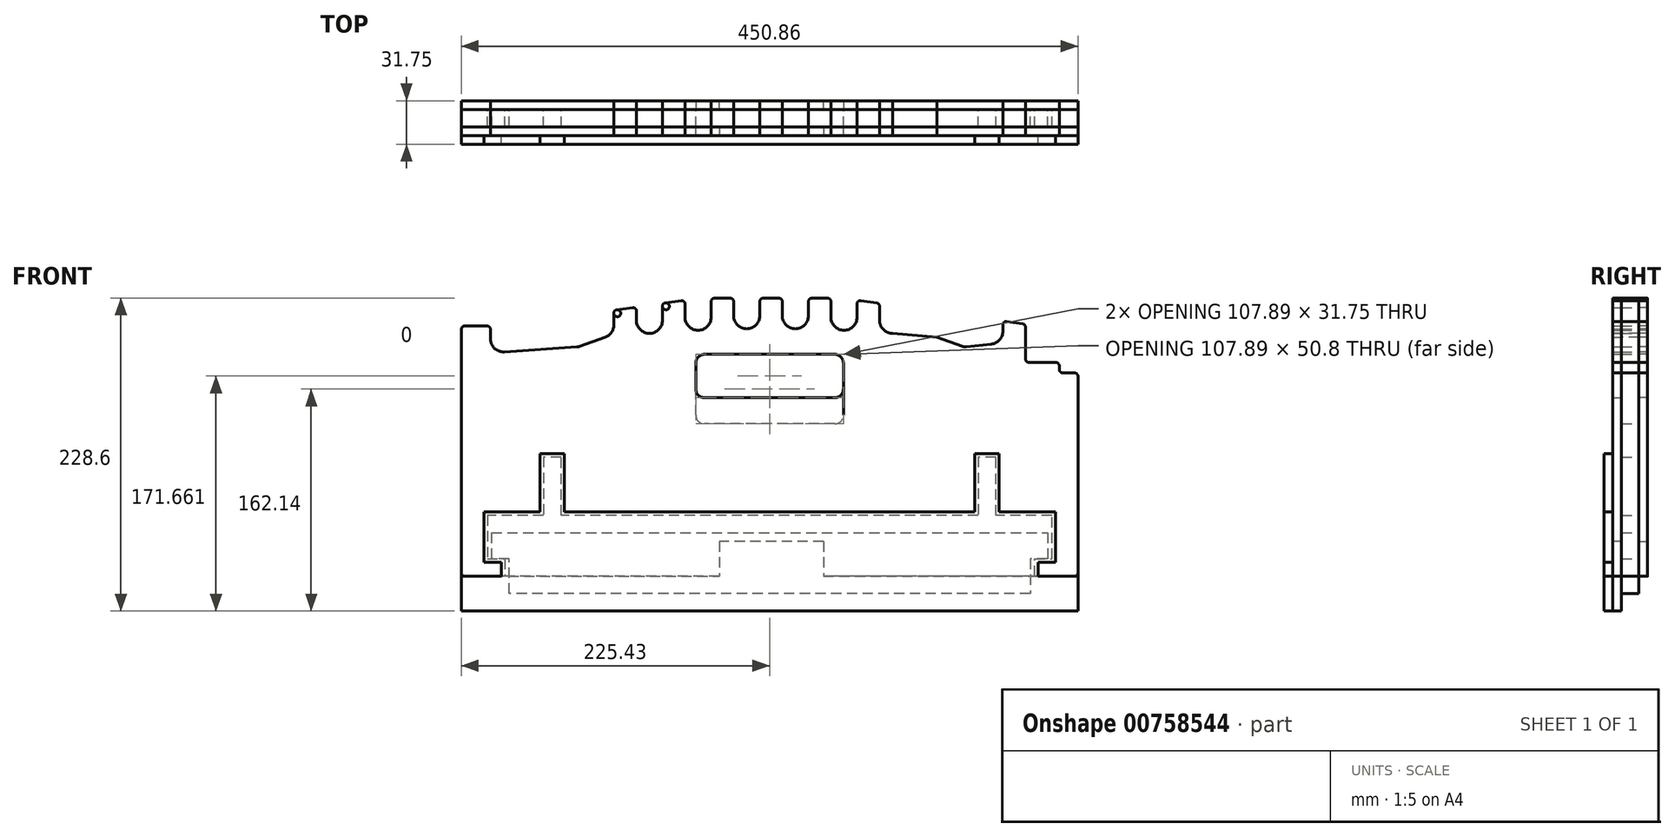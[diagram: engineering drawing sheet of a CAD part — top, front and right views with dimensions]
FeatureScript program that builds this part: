
annotation { "Feature Type Name" : "Feature", "Feature Type Description" : "" }
export const myFeature = defineFeature(function(context is Context, id is Id, definition is map)
    precondition{}
    {
        {
            var Q0;
            Q0=qCreatedBy(makeId("Front.planeOp"),FACE);
            var sketch = newSketch(context, id + "F0", { "sketchPlane" : qUnion([Q0])});
            skLineSegment(sketch, "E0", {"start": v(225.43, 44.45) * mm, "end": v(225.43, -101.6) * mm});
            skArc(sketch, "E1", {"start": v(225.42, 44.45) * mm, "mid": v(224.68, 46.25) * mm, "end": v(222.88, 47) * mm});
            skLineSegment(sketch, "E2", {"start": v(214.35, 47) * mm, "end": v(222.88, 47) * mm});
            skArc(sketch, "E3", {"start": v(211.8, 49.53) * mm, "mid": v(212.55, 47.73) * mm, "end": v(214.35, 47) * mm});
            skLineSegment(sketch, "E4", {"start": v(211.8, 52.07) * mm, "end": v(211.8, 49.53) * mm});
            skArc(sketch, "E5", {"start": v(211.8, 52.07) * mm, "mid": v(211.06, 53.87) * mm, "end": v(209.27, 54.6) * mm});
            skLineSegment(sketch, "E6", {"start": v(189.61, 54.61) * mm, "end": v(209.27, 54.61) * mm});
            skArc(sketch, "E7", {"start": v(187.07, 57.15) * mm, "mid": v(187.81, 55.35) * mm, "end": v(189.61, 54.61) * mm});
            skLineSegment(sketch, "E8", {"start": v(187.07, 80.43) * mm, "end": v(187.07, 57.15) * mm});
            skArc(sketch, "E9", {"start": v(187.07, 80.43) * mm, "mid": v(186.45, 82.1) * mm, "end": v(184.9, 82.94) * mm});
            skLineSegment(sketch, "E10", {"start": v(173.46, 84.58) * mm, "end": v(184.9, 82.94) * mm});
            skArc(sketch, "E11", {"start": v(173.46, 84.58) * mm, "mid": v(171.44, 83.98) * mm, "end": v(170.56, 82.06) * mm});
            skLineSegment(sketch, "E12", {"start": v(170.56, 77.52) * mm, "end": v(170.56, 82.06) * mm});
            skArc(sketch, "E13", {"start": v(162.11, 68.05) * mm, "mid": v(168.14, 71.17) * mm, "end": v(170.56, 77.52) * mm});
            skLineSegment(sketch, "E14", {"start": v(143.97, 65.99) * mm, "end": v(162.11, 68.05) * mm});
            skArc(sketch, "E15", {"start": v(141.12, 66.32) * mm, "mid": v(142.53, 65.99) * mm, "end": v(143.97, 65.99) * mm});
            skLineSegment(sketch, "E16", {"start": v(122.27, 73.06) * mm, "end": v(141.12, 66.32) * mm});
            skArc(sketch, "E17", {"start": v(115.95, 82.03) * mm, "mid": v(117.69, 76.54) * mm, "end": v(122.27, 73.06) * mm});
            skLineSegment(sketch, "E18", {"start": v(115.95, 90.6) * mm, "end": v(115.95, 82.03) * mm});
            skArc(sketch, "E19", {"start": v(115.95, 90.6) * mm, "mid": v(115.33, 92.26) * mm, "end": v(113.77, 93.1) * mm});
            skLineSegment(sketch, "E20", {"start": v(102.34, 94.74) * mm, "end": v(113.77, 93.1) * mm});
            skArc(sketch, "E21", {"start": v(102.34, 94.74) * mm, "mid": v(100.32, 94.14) * mm, "end": v(99.44, 92.22) * mm});
            skLineSegment(sketch, "E22", {"start": v(99.44, 85.4) * mm, "end": v(99.44, 92.22) * mm});
            skArc(sketch, "E23", {"start": v(80.4, 85.4) * mm, "mid": v(89.92, 75.87) * mm, "end": v(99.44, 85.4) * mm});
            skLineSegment(sketch, "E24", {"start": v(80.4, 95.67) * mm, "end": v(80.4, 85.4) * mm});
            skArc(sketch, "E25", {"start": v(80.4, 95.67) * mm, "mid": v(79.77, 97.34) * mm, "end": v(78.21, 98.19) * mm});
            skLineSegment(sketch, "E26", {"start": v(66.78, 99.82) * mm, "end": v(78.21, 98.19) * mm});
            skArc(sketch, "E27", {"start": v(66.78, 99.82) * mm, "mid": v(64.76, 99.22) * mm, "end": v(63.88, 97.3) * mm});
            skLineSegment(sketch, "E28", {"start": v(63.88, 87.64) * mm, "end": v(63.88, 97.3) * mm});
            skArc(sketch, "E29", {"start": v(44.83, 87.64) * mm, "mid": v(54.36, 78.12) * mm, "end": v(63.88, 87.64) * mm});
            skLineSegment(sketch, "E30", {"start": v(44.83, 99.06) * mm, "end": v(44.83, 87.64) * mm});
            skArc(sketch, "E31", {"start": v(44.83, 99.06) * mm, "mid": v(44.09, 100.86) * mm, "end": v(42.3, 101.6) * mm});
            skLineSegment(sketch, "E32", {"start": v(30.86, 101.6) * mm, "end": v(42.3, 101.6) * mm});
            skArc(sketch, "E33", {"start": v(30.86, 101.6) * mm, "mid": v(29.06, 100.86) * mm, "end": v(28.32, 99.06) * mm});
            skLineSegment(sketch, "E34", {"start": v(28.32, 88.76) * mm, "end": v(28.32, 99.06) * mm});
            skArc(sketch, "E35", {"start": v(9.27, 88.76) * mm, "mid": v(18.8, 79.24) * mm, "end": v(28.32, 88.76) * mm});
            skLineSegment(sketch, "E36", {"start": v(9.27, 99.06) * mm, "end": v(9.27, 88.76) * mm});
            skArc(sketch, "E37", {"start": v(9.27, 99.06) * mm, "mid": v(8.53, 100.86) * mm, "end": v(6.73, 101.6) * mm});
            skLineSegment(sketch, "E38", {"start": v(-4.7, 101.6) * mm, "end": v(6.73, 101.6) * mm});
            skArc(sketch, "E39", {"start": v(-4.7, 101.6) * mm, "mid": v(-6.5, 100.86) * mm, "end": v(-7.24, 99.06) * mm});
            skLineSegment(sketch, "E40", {"start": v(-7.24, 88.76) * mm, "end": v(-7.24, 99.06) * mm});
            skArc(sketch, "E41", {"start": v(-26.29, 88.76) * mm, "mid": v(-16.76, 79.24) * mm, "end": v(-7.24, 88.76) * mm});
            skLineSegment(sketch, "E42", {"start": v(-26.29, 99.06) * mm, "end": v(-26.29, 88.76) * mm});
            skArc(sketch, "E43", {"start": v(-26.29, 99.06) * mm, "mid": v(-27.03, 100.86) * mm, "end": v(-28.83, 101.6) * mm});
            skLineSegment(sketch, "E44", {"start": v(-40.26, 101.6) * mm, "end": v(-28.83, 101.6) * mm});
            skArc(sketch, "E45", {"start": v(-40.26, 101.6) * mm, "mid": v(-42.06, 100.86) * mm, "end": v(-42.8, 99.06) * mm});
            skLineSegment(sketch, "E46", {"start": v(-42.8, 87.64) * mm, "end": v(-42.8, 99.06) * mm});
            skArc(sketch, "E47", {"start": v(-61.85, 87.64) * mm, "mid": v(-52.32, 78.12) * mm, "end": v(-42.8, 87.64) * mm});
            skLineSegment(sketch, "E48", {"start": v(-61.85, 97.3) * mm, "end": v(-61.85, 87.64) * mm});
            skArc(sketch, "E49", {"start": v(-61.85, 97.3) * mm, "mid": v(-62.72, 99.23) * mm, "end": v(-64.75, 99.82) * mm});
            skLineSegment(sketch, "E50", {"start": v(-76.18, 98.19) * mm, "end": v(-64.75, 99.82) * mm});
            skArc(sketch, "E51", {"start": v(-76.18, 98.19) * mm, "mid": v(-77.74, 97.34) * mm, "end": v(-78.36, 95.67) * mm});
            skLineSegment(sketch, "E52", {"start": v(-78.36, 85.4) * mm, "end": v(-78.36, 95.67) * mm});
            skArc(sketch, "E53", {"start": v(-97.4, 85.4) * mm, "mid": v(-87.88, 75.87) * mm, "end": v(-78.36, 85.4) * mm});
            skLineSegment(sketch, "E54", {"start": v(-97.4, 92.23) * mm, "end": v(-97.4, 85.4) * mm});
            skArc(sketch, "E55", {"start": v(-97.4, 92.23) * mm, "mid": v(-98.28, 94.15) * mm, "end": v(-100.3, 94.74) * mm});
            skLineSegment(sketch, "E56", {"start": v(-111.74, 93.1) * mm, "end": v(-100.3, 94.74) * mm});
            skArc(sketch, "E57", {"start": v(-111.74, 93.1) * mm, "mid": v(-113.3, 92.26) * mm, "end": v(-113.92, 90.6) * mm});
            skLineSegment(sketch, "E58", {"start": v(-113.92, 82.03) * mm, "end": v(-113.92, 90.6) * mm});
            skArc(sketch, "E59", {"start": v(-120.24, 73.06) * mm, "mid": v(-115.66, 76.54) * mm, "end": v(-113.92, 82.03) * mm});
            skLineSegment(sketch, "E60", {"start": v(-139.09, 66.32) * mm, "end": v(-120.24, 73.06) * mm});
            skArc(sketch, "E61", {"start": v(-140.8, 65.96) * mm, "mid": v(-139.93, 66.08) * mm, "end": v(-139.09, 66.32) * mm});
            skLineSegment(sketch, "E62", {"start": v(-193.92, 62.35) * mm, "end": v(-140.8, 65.96) * mm});
            skArc(sketch, "E63", {"start": v(-204.09, 71.85) * mm, "mid": v(-201.07, 64.9) * mm, "end": v(-193.92, 62.35) * mm});
            skLineSegment(sketch, "E64", {"start": v(-204.09, 78.74) * mm, "end": v(-204.09, 71.85) * mm});
            skArc(sketch, "E65", {"start": v(-204.09, 78.74) * mm, "mid": v(-204.83, 80.54) * mm, "end": v(-206.63, 81.28) * mm});
            skLineSegment(sketch, "E66", {"start": v(-222.89, 81.28) * mm, "end": v(-206.63, 81.28) * mm});
            skArc(sketch, "E67", {"start": v(-222.89, 81.28) * mm, "mid": v(-224.68, 80.54) * mm, "end": v(-225.43, 78.74) * mm});
            skLineSegment(sketch, "E68", {"start": v(-225.43, -101.6) * mm, "end": v(-225.43, 78.74) * mm});
            skLineSegment(sketch, "E69", {"start": v(-193.68, -101.6) * mm, "end": v(-225.43, -101.6) * mm});
            skLineSegment(sketch, "E70", {"start": v(-193.68, -88.9) * mm, "end": v(-193.68, -101.6) * mm});
            skLineSegment(sketch, "E71", {"start": v(-206.38, -88.9) * mm, "end": v(-193.68, -88.9) * mm});
            skLineSegment(sketch, "E72", {"start": v(-206.38, -57.15) * mm, "end": v(-206.38, -88.9) * mm});
            skLineSegment(sketch, "E73", {"start": v(-165.35, -57.15) * mm, "end": v(-206.38, -57.15) * mm});
            skLineSegment(sketch, "E74", {"start": v(-165.35, -14.48) * mm, "end": v(-165.35, -57.15) * mm});
            skLineSegment(sketch, "E75", {"start": v(-152.4, -14.48) * mm, "end": v(-165.35, -14.48) * mm});
            skLineSegment(sketch, "E76", {"start": v(-152.4, -57.15) * mm, "end": v(-152.4, -14.48) * mm});
            skLineSegment(sketch, "E77", {"start": v(152.4, -57.15) * mm, "end": v(-152.4, -57.15) * mm});
            skLineSegment(sketch, "E78", {"start": v(152.4, -14.48) * mm, "end": v(152.4, -57.15) * mm});
            skLineSegment(sketch, "E79", {"start": v(165.35, -14.48) * mm, "end": v(152.4, -14.48) * mm});
            skLineSegment(sketch, "E80", {"start": v(165.35, -57.15) * mm, "end": v(165.35, -14.48) * mm});
            skLineSegment(sketch, "E81", {"start": v(206.38, -57.15) * mm, "end": v(165.35, -57.15) * mm});
            skLineSegment(sketch, "E82", {"start": v(206.38, -88.9) * mm, "end": v(206.38, -57.15) * mm});
            skLineSegment(sketch, "E83", {"start": v(193.68, -88.9) * mm, "end": v(206.38, -88.9) * mm});
            skLineSegment(sketch, "E84", {"start": v(193.68, -101.6) * mm, "end": v(193.68, -88.9) * mm});
            skLineSegment(sketch, "E85", {"start": v(225.43, -101.6) * mm, "end": v(193.68, -101.6) * mm});
            skLineSegment(sketch, "E86", {"start": v(47.6, 9.74) * mm, "end": v(-47.6, 9.74) * mm});
            skArc(sketch, "E87", {"start": v(-53.95, 16.1) * mm, "mid": v(-52.09, 11.6) * mm, "end": v(-47.6, 9.74) * mm});
            skLineSegment(sketch, "E88", {"start": v(-53.95, 16.1) * mm, "end": v(-53.95, 54.2) * mm});
            skArc(sketch, "E89", {"start": v(-47.6, 60.54) * mm, "mid": v(-52.09, 58.68) * mm, "end": v(-53.95, 54.2) * mm});
            skLineSegment(sketch, "E90", {"start": v(-47.6, 60.54) * mm, "end": v(47.6, 60.54) * mm});
            skArc(sketch, "E91", {"start": v(53.95, 54.2) * mm, "mid": v(52.09, 58.68) * mm, "end": v(47.6, 60.54) * mm});
            skLineSegment(sketch, "E92", {"start": v(53.95, 54.2) * mm, "end": v(53.95, 16.1) * mm});
            skArc(sketch, "E93", {"start": v(47.6, 9.74) * mm, "mid": v(52.09, 11.6) * mm, "end": v(53.95, 16.1) * mm});
            skLineSegment(sketch, "E94", {"start": v(225.43, -101.6) * mm, "end": v(-225.43, -101.6) * mm, "construction": true});
            skLineSegment(sketch, "E95", {"start": v(-225.43, -101.6) * mm, "end": v(-225.43, 0) * mm, "construction": true});
            skLineSegment(sketch, "E96", {"start": v(-225.43, 0) * mm, "end": v(225.43, 0) * mm, "construction": true});
            skLineSegment(sketch, "E97", {"start": v(225.43, 0) * mm, "end": v(225.43, -101.6) * mm, "construction": true});
            skSolve(sketch);
        }
        {
            var Q0;
            Q0=qSketchRegion(id+"F0",true);
            extrude(context, id + "F1", {"entities" : qUnion([Q0]), "depth" : 12.7 * mm});
        }
        {
            var Q0;
            Q0=makeQuery(id+"F1.opExtrude","CAP_FACE",FACE,{"disambiguationData":[OSD([sQuery(id+"F0.wireOp",EDGE,"f3b8bc04-095d-494a-bcce-8306202adf07"),sQuery(id+"F0.wireOp",EDGE,"08e92012-2e21-4d94-9f0a-c8e57075e395"),sQuery(id+"F0.wireOp",EDGE,"122fa739-26d1-4298-ae19-82ac91bd4e23"),sQuery(id+"F0.wireOp",EDGE,"d5e32c5b-27bd-42dd-9b3f-d947ba78b5c6"),sQuery(id+"F0.wireOp",EDGE,"E0"),sQuery(id+"F0.wireOp",EDGE,"E1"),sQuery(id+"F0.wireOp",EDGE,"E2"),sQuery(id+"F0.wireOp",EDGE,"E3"),sQuery(id+"F0.wireOp",EDGE,"E4"),sQuery(id+"F0.wireOp",EDGE,"E5"),sQuery(id+"F0.wireOp",EDGE,"E6"),sQuery(id+"F0.wireOp",EDGE,"E7"),sQuery(id+"F0.wireOp",EDGE,"E8"),sQuery(id+"F0.wireOp",EDGE,"E9"),sQuery(id+"F0.wireOp",EDGE,"E10"),sQuery(id+"F0.wireOp",EDGE,"E11"),sQuery(id+"F0.wireOp",EDGE,"E12"),sQuery(id+"F0.wireOp",EDGE,"E13"),sQuery(id+"F0.wireOp",EDGE,"E14"),sQuery(id+"F0.wireOp",EDGE,"E15"),sQuery(id+"F0.wireOp",EDGE,"E16"),sQuery(id+"F0.wireOp",EDGE,"E17"),sQuery(id+"F0.wireOp",EDGE,"E18"),sQuery(id+"F0.wireOp",EDGE,"E19"),sQuery(id+"F0.wireOp",EDGE,"E20"),sQuery(id+"F0.wireOp",EDGE,"E21"),sQuery(id+"F0.wireOp",EDGE,"E22"),sQuery(id+"F0.wireOp",EDGE,"E23"),sQuery(id+"F0.wireOp",EDGE,"E24"),sQuery(id+"F0.wireOp",EDGE,"E25"),sQuery(id+"F0.wireOp",EDGE,"E26"),sQuery(id+"F0.wireOp",EDGE,"E27"),sQuery(id+"F0.wireOp",EDGE,"E28"),sQuery(id+"F0.wireOp",EDGE,"E29"),sQuery(id+"F0.wireOp",EDGE,"E30"),sQuery(id+"F0.wireOp",EDGE,"E31"),sQuery(id+"F0.wireOp",EDGE,"E32"),sQuery(id+"F0.wireOp",EDGE,"E33"),sQuery(id+"F0.wireOp",EDGE,"E34"),sQuery(id+"F0.wireOp",EDGE,"E35"),sQuery(id+"F0.wireOp",EDGE,"E36"),sQuery(id+"F0.wireOp",EDGE,"E37"),sQuery(id+"F0.wireOp",EDGE,"E38"),sQuery(id+"F0.wireOp",EDGE,"E39"),sQuery(id+"F0.wireOp",EDGE,"E40"),sQuery(id+"F0.wireOp",EDGE,"E41"),sQuery(id+"F0.wireOp",EDGE,"E42"),sQuery(id+"F0.wireOp",EDGE,"E43"),sQuery(id+"F0.wireOp",EDGE,"E44"),sQuery(id+"F0.wireOp",EDGE,"E45"),sQuery(id+"F0.wireOp",EDGE,"E46"),sQuery(id+"F0.wireOp",EDGE,"E47"),sQuery(id+"F0.wireOp",EDGE,"E48"),sQuery(id+"F0.wireOp",EDGE,"E49"),sQuery(id+"F0.wireOp",EDGE,"E50"),sQuery(id+"F0.wireOp",EDGE,"E51"),sQuery(id+"F0.wireOp",EDGE,"E52"),sQuery(id+"F0.wireOp",EDGE,"E53"),sQuery(id+"F0.wireOp",EDGE,"E54"),sQuery(id+"F0.wireOp",EDGE,"E55"),sQuery(id+"F0.wireOp",EDGE,"E56"),sQuery(id+"F0.wireOp",EDGE,"E57"),sQuery(id+"F0.wireOp",EDGE,"E58"),sQuery(id+"F0.wireOp",EDGE,"E59"),sQuery(id+"F0.wireOp",EDGE,"E60"),sQuery(id+"F0.wireOp",EDGE,"E61"),sQuery(id+"F0.wireOp",EDGE,"E62"),sQuery(id+"F0.wireOp",EDGE,"E63"),sQuery(id+"F0.wireOp",EDGE,"E64"),sQuery(id+"F0.wireOp",EDGE,"E65"),sQuery(id+"F0.wireOp",EDGE,"E66"),sQuery(id+"F0.wireOp",EDGE,"E67"),sQuery(id+"F0.wireOp",EDGE,"E68"),sQuery(id+"F0.wireOp",EDGE,"E69"),sQuery(id+"F0.wireOp",EDGE,"E70"),sQuery(id+"F0.wireOp",EDGE,"E71"),sQuery(id+"F0.wireOp",EDGE,"E72"),sQuery(id+"F0.wireOp",EDGE,"E73"),sQuery(id+"F0.wireOp",EDGE,"E74"),sQuery(id+"F0.wireOp",EDGE,"E75"),sQuery(id+"F0.wireOp",EDGE,"E76"),sQuery(id+"F0.wireOp",EDGE,"E77"),sQuery(id+"F0.wireOp",EDGE,"E78"),sQuery(id+"F0.wireOp",EDGE,"E79"),sQuery(id+"F0.wireOp",EDGE,"E80"),sQuery(id+"F0.wireOp",EDGE,"E81"),sQuery(id+"F0.wireOp",EDGE,"E82"),sQuery(id+"F0.wireOp",EDGE,"E83"),sQuery(id+"F0.wireOp",EDGE,"E84"),sQuery(id+"F0.wireOp",EDGE,"E85"),sQuery(id+"F0.wireOp",EDGE,"2d70706d-4c91-45b7-b293-bf747273fc1e"),sQuery(id+"F0.wireOp",EDGE,"f606c3c6-6e26-49ba-bb4a-ffbf22b89f78"),sQuery(id+"F0.wireOp",EDGE,"6ded5a20-7a3f-46e3-8459-1bb58dbc2f72"),sQuery(id+"F0.wireOp",EDGE,"099ca5a8-81e7-49d1-b38d-3a86f93f5891"),sQuery(id+"F0.wireOp",EDGE,"E86"),sQuery(id+"F0.wireOp",EDGE,"E87"),sQuery(id+"F0.wireOp",EDGE,"E88"),sQuery(id+"F0.wireOp",EDGE,"E89"),sQuery(id+"F0.wireOp",EDGE,"E90"),sQuery(id+"F0.wireOp",EDGE,"E91"),sQuery(id+"F0.wireOp",EDGE,"E92"),sQuery(id+"F0.wireOp",EDGE,"E93")])],"isStart":true});
            cPlane(context, id + "F2", {"entities" : qUnion([Q0]), "cplaneType" : CPlaneType.OFFSET, "offset" : 0 * mm, "oppositeDirection" : true, "width" : 152.4 * mm, "height" : 152.4 * mm});
        }
        {
            var Q0;
            Q0=qCreatedBy(id+"F2.planeOp",FACE);
            var sketch = newSketch(context, id + "F3", { "sketchPlane" : qUnion([Q0])});
            skLineSegment(sketch, "E98", {"start": v(-203.2, -69.85) * mm, "end": v(-203.2, -88.9) * mm});
            skLineSegment(sketch, "E99", {"start": v(-203.2, -88.9) * mm, "end": v(-190.5, -88.9) * mm});
            skLineSegment(sketch, "E100", {"start": v(-190.5, -88.9) * mm, "end": v(-190.5, -114.3) * mm});
            skLineSegment(sketch, "E101", {"start": v(-190.5, -114.3) * mm, "end": v(190.5, -114.3) * mm});
            skLineSegment(sketch, "E102", {"start": v(190.5, -114.3) * mm, "end": v(190.5, -88.9) * mm});
            skLineSegment(sketch, "E103", {"start": v(190.5, -88.9) * mm, "end": v(203.2, -88.9) * mm});
            skLineSegment(sketch, "E104", {"start": v(203.2, -88.9) * mm, "end": v(203.2, -69.85) * mm});
            skLineSegment(sketch, "E105", {"start": v(203.2, -69.85) * mm, "end": v(-203.2, -69.85) * mm});
            skSolve(sketch);
        }
        {
            var Q0;
            Q0=qSketchRegion(id+"F3",true);
            extrude(context, id + "F4", {"entities" : qUnion([Q0]), "oppositeDirection" : true, "depth" : 12.7 * mm});
        }
        {
            var Q0;
            Q0=makeQuery(id+"F1.opExtrude","CAP_FACE",FACE,{"disambiguationData":[OSD([sQuery(id+"F0.wireOp",EDGE,"f3b8bc04-095d-494a-bcce-8306202adf07"),sQuery(id+"F0.wireOp",EDGE,"08e92012-2e21-4d94-9f0a-c8e57075e395"),sQuery(id+"F0.wireOp",EDGE,"122fa739-26d1-4298-ae19-82ac91bd4e23"),sQuery(id+"F0.wireOp",EDGE,"d5e32c5b-27bd-42dd-9b3f-d947ba78b5c6"),sQuery(id+"F0.wireOp",EDGE,"E0"),sQuery(id+"F0.wireOp",EDGE,"E1"),sQuery(id+"F0.wireOp",EDGE,"E2"),sQuery(id+"F0.wireOp",EDGE,"E3"),sQuery(id+"F0.wireOp",EDGE,"E4"),sQuery(id+"F0.wireOp",EDGE,"E5"),sQuery(id+"F0.wireOp",EDGE,"E6"),sQuery(id+"F0.wireOp",EDGE,"E7"),sQuery(id+"F0.wireOp",EDGE,"E8"),sQuery(id+"F0.wireOp",EDGE,"E9"),sQuery(id+"F0.wireOp",EDGE,"E10"),sQuery(id+"F0.wireOp",EDGE,"E11"),sQuery(id+"F0.wireOp",EDGE,"E12"),sQuery(id+"F0.wireOp",EDGE,"E13"),sQuery(id+"F0.wireOp",EDGE,"E14"),sQuery(id+"F0.wireOp",EDGE,"E15"),sQuery(id+"F0.wireOp",EDGE,"E16"),sQuery(id+"F0.wireOp",EDGE,"E17"),sQuery(id+"F0.wireOp",EDGE,"E18"),sQuery(id+"F0.wireOp",EDGE,"E19"),sQuery(id+"F0.wireOp",EDGE,"E20"),sQuery(id+"F0.wireOp",EDGE,"E21"),sQuery(id+"F0.wireOp",EDGE,"E22"),sQuery(id+"F0.wireOp",EDGE,"E23"),sQuery(id+"F0.wireOp",EDGE,"E24"),sQuery(id+"F0.wireOp",EDGE,"E25"),sQuery(id+"F0.wireOp",EDGE,"E26"),sQuery(id+"F0.wireOp",EDGE,"E27"),sQuery(id+"F0.wireOp",EDGE,"E28"),sQuery(id+"F0.wireOp",EDGE,"E29"),sQuery(id+"F0.wireOp",EDGE,"E30"),sQuery(id+"F0.wireOp",EDGE,"E31"),sQuery(id+"F0.wireOp",EDGE,"E32"),sQuery(id+"F0.wireOp",EDGE,"E33"),sQuery(id+"F0.wireOp",EDGE,"E34"),sQuery(id+"F0.wireOp",EDGE,"E35"),sQuery(id+"F0.wireOp",EDGE,"E36"),sQuery(id+"F0.wireOp",EDGE,"E37"),sQuery(id+"F0.wireOp",EDGE,"E38"),sQuery(id+"F0.wireOp",EDGE,"E39"),sQuery(id+"F0.wireOp",EDGE,"E40"),sQuery(id+"F0.wireOp",EDGE,"E41"),sQuery(id+"F0.wireOp",EDGE,"E42"),sQuery(id+"F0.wireOp",EDGE,"E43"),sQuery(id+"F0.wireOp",EDGE,"E44"),sQuery(id+"F0.wireOp",EDGE,"E45"),sQuery(id+"F0.wireOp",EDGE,"E46"),sQuery(id+"F0.wireOp",EDGE,"E47"),sQuery(id+"F0.wireOp",EDGE,"E48"),sQuery(id+"F0.wireOp",EDGE,"E49"),sQuery(id+"F0.wireOp",EDGE,"E50"),sQuery(id+"F0.wireOp",EDGE,"E51"),sQuery(id+"F0.wireOp",EDGE,"E52"),sQuery(id+"F0.wireOp",EDGE,"E53"),sQuery(id+"F0.wireOp",EDGE,"E54"),sQuery(id+"F0.wireOp",EDGE,"E55"),sQuery(id+"F0.wireOp",EDGE,"E56"),sQuery(id+"F0.wireOp",EDGE,"E57"),sQuery(id+"F0.wireOp",EDGE,"E58"),sQuery(id+"F0.wireOp",EDGE,"E59"),sQuery(id+"F0.wireOp",EDGE,"E60"),sQuery(id+"F0.wireOp",EDGE,"E61"),sQuery(id+"F0.wireOp",EDGE,"E62"),sQuery(id+"F0.wireOp",EDGE,"E63"),sQuery(id+"F0.wireOp",EDGE,"E64"),sQuery(id+"F0.wireOp",EDGE,"E65"),sQuery(id+"F0.wireOp",EDGE,"E66"),sQuery(id+"F0.wireOp",EDGE,"E67"),sQuery(id+"F0.wireOp",EDGE,"E68"),sQuery(id+"F0.wireOp",EDGE,"E69"),sQuery(id+"F0.wireOp",EDGE,"E70"),sQuery(id+"F0.wireOp",EDGE,"E71"),sQuery(id+"F0.wireOp",EDGE,"E72"),sQuery(id+"F0.wireOp",EDGE,"E73"),sQuery(id+"F0.wireOp",EDGE,"E74"),sQuery(id+"F0.wireOp",EDGE,"E75"),sQuery(id+"F0.wireOp",EDGE,"E76"),sQuery(id+"F0.wireOp",EDGE,"E77"),sQuery(id+"F0.wireOp",EDGE,"E78"),sQuery(id+"F0.wireOp",EDGE,"E79"),sQuery(id+"F0.wireOp",EDGE,"E80"),sQuery(id+"F0.wireOp",EDGE,"E81"),sQuery(id+"F0.wireOp",EDGE,"E82"),sQuery(id+"F0.wireOp",EDGE,"E83"),sQuery(id+"F0.wireOp",EDGE,"E84"),sQuery(id+"F0.wireOp",EDGE,"E85"),sQuery(id+"F0.wireOp",EDGE,"2d70706d-4c91-45b7-b293-bf747273fc1e"),sQuery(id+"F0.wireOp",EDGE,"f606c3c6-6e26-49ba-bb4a-ffbf22b89f78"),sQuery(id+"F0.wireOp",EDGE,"6ded5a20-7a3f-46e3-8459-1bb58dbc2f72"),sQuery(id+"F0.wireOp",EDGE,"099ca5a8-81e7-49d1-b38d-3a86f93f5891"),sQuery(id+"F0.wireOp",EDGE,"E86"),sQuery(id+"F0.wireOp",EDGE,"E87"),sQuery(id+"F0.wireOp",EDGE,"E88"),sQuery(id+"F0.wireOp",EDGE,"E89"),sQuery(id+"F0.wireOp",EDGE,"E90"),sQuery(id+"F0.wireOp",EDGE,"E91"),sQuery(id+"F0.wireOp",EDGE,"E92"),sQuery(id+"F0.wireOp",EDGE,"E93")])],"isStart":true});
            cPlane(context, id + "F5", {"entities" : qUnion([Q0]), "cplaneType" : CPlaneType.OFFSET, "offset" : 6.35 * mm, "oppositeDirection" : true, "width" : 152.4 * mm, "height" : 152.4 * mm});
        }
        {
            var Q0;
            Q0=qCreatedBy(id+"F2.planeOp",FACE);
            var sketch = newSketch(context, id + "F6", { "sketchPlane" : qUnion([Q0])});
            skLineSegment(sketch, "E106", {"start": v(-225.43, 44.45) * mm, "end": v(-225.43, -99.06) * mm});
            skArc(sketch, "E107", {"start": v(-225.43, -99.06) * mm, "mid": v(-224.68, -100.86) * mm, "end": v(-222.89, -101.6) * mm});
            skLineSegment(sketch, "E108", {"start": v(-222.89, -101.6) * mm, "end": v(222.88, -101.6) * mm});
            skArc(sketch, "E109", {"start": v(222.88, -101.6) * mm, "mid": v(224.68, -100.86) * mm, "end": v(225.42, -99.06) * mm});
            skLineSegment(sketch, "E110", {"start": v(225.43, -99.06) * mm, "end": v(225.43, 78.74) * mm});
            skArc(sketch, "E111", {"start": v(225.42, 78.74) * mm, "mid": v(224.68, 80.54) * mm, "end": v(222.88, 81.28) * mm});
            skLineSegment(sketch, "E112", {"start": v(222.88, 81.28) * mm, "end": v(206.63, 81.28) * mm});
            skArc(sketch, "E113", {"start": v(206.63, 81.28) * mm, "mid": v(204.83, 80.54) * mm, "end": v(204.09, 78.74) * mm});
            skLineSegment(sketch, "E114", {"start": v(204.09, 78.74) * mm, "end": v(204.09, 71.85) * mm});
            skArc(sketch, "E115", {"start": v(193.92, 62.35) * mm, "mid": v(201.07, 64.9) * mm, "end": v(204.09, 71.85) * mm});
            skLineSegment(sketch, "E116", {"start": v(193.92, 62.35) * mm, "end": v(140.8, 65.96) * mm});
            skArc(sketch, "E117", {"start": v(139.09, 66.32) * mm, "mid": v(139.93, 66.08) * mm, "end": v(140.8, 65.96) * mm});
            skLineSegment(sketch, "E118", {"start": v(139.09, 66.32) * mm, "end": v(120.24, 73.06) * mm});
            skArc(sketch, "E119", {"start": v(113.92, 82.03) * mm, "mid": v(115.66, 76.54) * mm, "end": v(120.24, 73.06) * mm});
            skLineSegment(sketch, "E120", {"start": v(113.92, 82.03) * mm, "end": v(113.92, 90.6) * mm});
            skArc(sketch, "E121", {"start": v(113.92, 90.6) * mm, "mid": v(113.3, 92.26) * mm, "end": v(111.74, 93.1) * mm});
            skLineSegment(sketch, "E122", {"start": v(111.74, 93.1) * mm, "end": v(100.3, 94.74) * mm});
            skArc(sketch, "E123", {"start": v(100.3, 94.74) * mm, "mid": v(98.28, 94.15) * mm, "end": v(97.4, 92.23) * mm});
            skLineSegment(sketch, "E124", {"start": v(97.4, 92.23) * mm, "end": v(97.4, 85.4) * mm});
            skArc(sketch, "E125", {"start": v(78.36, 85.4) * mm, "mid": v(87.88, 75.87) * mm, "end": v(97.4, 85.4) * mm});
            skLineSegment(sketch, "E126", {"start": v(78.36, 85.4) * mm, "end": v(78.36, 95.67) * mm});
            skArc(sketch, "E127", {"start": v(78.36, 95.67) * mm, "mid": v(77.74, 97.34) * mm, "end": v(76.18, 98.19) * mm});
            skLineSegment(sketch, "E128", {"start": v(76.18, 98.19) * mm, "end": v(64.75, 99.82) * mm});
            skArc(sketch, "E129", {"start": v(64.75, 99.82) * mm, "mid": v(62.72, 99.23) * mm, "end": v(61.85, 97.3) * mm});
            skLineSegment(sketch, "E130", {"start": v(61.85, 97.3) * mm, "end": v(61.85, 87.64) * mm});
            skArc(sketch, "E131", {"start": v(42.8, 87.64) * mm, "mid": v(52.32, 78.12) * mm, "end": v(61.85, 87.64) * mm});
            skLineSegment(sketch, "E132", {"start": v(42.8, 87.64) * mm, "end": v(42.8, 99.06) * mm});
            skArc(sketch, "E133", {"start": v(42.8, 99.06) * mm, "mid": v(42.06, 100.86) * mm, "end": v(40.26, 101.6) * mm});
            skLineSegment(sketch, "E134", {"start": v(40.26, 101.6) * mm, "end": v(28.83, 101.6) * mm});
            skArc(sketch, "E135", {"start": v(28.83, 101.6) * mm, "mid": v(27.03, 100.86) * mm, "end": v(26.29, 99.06) * mm});
            skLineSegment(sketch, "E136", {"start": v(26.29, 99.06) * mm, "end": v(26.29, 88.76) * mm});
            skArc(sketch, "E137", {"start": v(7.24, 88.76) * mm, "mid": v(16.76, 79.24) * mm, "end": v(26.29, 88.76) * mm});
            skLineSegment(sketch, "E138", {"start": v(7.24, 88.76) * mm, "end": v(7.24, 99.06) * mm});
            skArc(sketch, "E139", {"start": v(7.24, 99.06) * mm, "mid": v(6.5, 100.86) * mm, "end": v(4.7, 101.6) * mm});
            skLineSegment(sketch, "E140", {"start": v(4.7, 101.6) * mm, "end": v(-6.73, 101.6) * mm});
            skArc(sketch, "E141", {"start": v(-6.73, 101.6) * mm, "mid": v(-8.53, 100.86) * mm, "end": v(-9.27, 99.06) * mm});
            skLineSegment(sketch, "E142", {"start": v(-9.27, 99.06) * mm, "end": v(-9.27, 88.76) * mm});
            skArc(sketch, "E143", {"start": v(-28.32, 88.76) * mm, "mid": v(-18.8, 79.24) * mm, "end": v(-9.27, 88.76) * mm});
            skLineSegment(sketch, "E144", {"start": v(-28.32, 88.76) * mm, "end": v(-28.32, 99.06) * mm});
            skArc(sketch, "E145", {"start": v(-28.32, 99.06) * mm, "mid": v(-29.06, 100.86) * mm, "end": v(-30.86, 101.6) * mm});
            skLineSegment(sketch, "E146", {"start": v(-30.86, 101.6) * mm, "end": v(-42.3, 101.6) * mm});
            skArc(sketch, "E147", {"start": v(-42.3, 101.6) * mm, "mid": v(-44.09, 100.86) * mm, "end": v(-44.83, 99.06) * mm});
            skLineSegment(sketch, "E148", {"start": v(-44.83, 99.06) * mm, "end": v(-44.83, 87.64) * mm});
            skArc(sketch, "E149", {"start": v(-63.88, 87.64) * mm, "mid": v(-54.36, 78.12) * mm, "end": v(-44.83, 87.64) * mm});
            skLineSegment(sketch, "E150", {"start": v(-63.88, 87.64) * mm, "end": v(-63.88, 97.3) * mm});
            skArc(sketch, "E151", {"start": v(-63.88, 97.3) * mm, "mid": v(-64.76, 99.22) * mm, "end": v(-66.78, 99.82) * mm});
            skLineSegment(sketch, "E152", {"start": v(-66.78, 99.82) * mm, "end": v(-78.21, 98.19) * mm});
            skArc(sketch, "E153", {"start": v(-78.21, 98.19) * mm, "mid": v(-79.77, 97.34) * mm, "end": v(-80.4, 95.67) * mm});
            skLineSegment(sketch, "E154", {"start": v(-80.4, 95.67) * mm, "end": v(-80.4, 85.4) * mm});
            skArc(sketch, "E155", {"start": v(-99.44, 85.4) * mm, "mid": v(-89.92, 75.87) * mm, "end": v(-80.4, 85.4) * mm});
            skLineSegment(sketch, "E156", {"start": v(-99.44, 85.4) * mm, "end": v(-99.44, 92.22) * mm});
            skArc(sketch, "E157", {"start": v(-99.44, 92.22) * mm, "mid": v(-100.32, 94.14) * mm, "end": v(-102.34, 94.74) * mm});
            skLineSegment(sketch, "E158", {"start": v(-102.34, 94.74) * mm, "end": v(-113.77, 93.1) * mm});
            skArc(sketch, "E159", {"start": v(-113.77, 93.1) * mm, "mid": v(-115.33, 92.26) * mm, "end": v(-115.95, 90.6) * mm});
            skLineSegment(sketch, "E160", {"start": v(-115.95, 90.6) * mm, "end": v(-115.95, 82.03) * mm});
            skArc(sketch, "E161", {"start": v(-122.27, 73.06) * mm, "mid": v(-117.69, 76.54) * mm, "end": v(-115.95, 82.03) * mm});
            skLineSegment(sketch, "E162", {"start": v(-122.27, 73.06) * mm, "end": v(-141.12, 66.32) * mm});
            skArc(sketch, "E163", {"start": v(-143.97, 65.99) * mm, "mid": v(-142.53, 65.99) * mm, "end": v(-141.12, 66.32) * mm});
            skLineSegment(sketch, "E164", {"start": v(-143.97, 65.99) * mm, "end": v(-162.11, 68.05) * mm});
            skArc(sketch, "E165", {"start": v(-170.56, 77.52) * mm, "mid": v(-168.14, 71.17) * mm, "end": v(-162.11, 68.05) * mm});
            skLineSegment(sketch, "E166", {"start": v(-170.56, 77.52) * mm, "end": v(-170.56, 82.06) * mm});
            skArc(sketch, "E167", {"start": v(-170.56, 82.06) * mm, "mid": v(-171.44, 83.98) * mm, "end": v(-173.46, 84.58) * mm});
            skLineSegment(sketch, "E168", {"start": v(-173.46, 84.58) * mm, "end": v(-184.9, 82.94) * mm});
            skArc(sketch, "E169", {"start": v(-184.9, 82.94) * mm, "mid": v(-186.45, 82.1) * mm, "end": v(-187.07, 80.43) * mm});
            skLineSegment(sketch, "E170", {"start": v(-187.07, 80.43) * mm, "end": v(-187.07, 57.15) * mm});
            skArc(sketch, "E171", {"start": v(-189.61, 54.61) * mm, "mid": v(-187.81, 55.35) * mm, "end": v(-187.07, 57.15) * mm});
            skLineSegment(sketch, "E172", {"start": v(-189.61, 54.61) * mm, "end": v(-209.27, 54.61) * mm});
            skArc(sketch, "E173", {"start": v(-209.27, 54.6) * mm, "mid": v(-211.06, 53.87) * mm, "end": v(-211.8, 52.07) * mm});
            skLineSegment(sketch, "E174", {"start": v(-211.8, 52.07) * mm, "end": v(-211.8, 49.53) * mm});
            skArc(sketch, "E175", {"start": v(-214.35, 47) * mm, "mid": v(-212.55, 47.73) * mm, "end": v(-211.8, 49.53) * mm});
            skLineSegment(sketch, "E176", {"start": v(-214.35, 47) * mm, "end": v(-222.89, 47) * mm});
            skArc(sketch, "E177", {"start": v(-222.89, 47) * mm, "mid": v(-224.68, 46.25) * mm, "end": v(-225.43, 44.45) * mm});
            skLineSegment(sketch, "E178", {"start": v(-47.6, 28.79) * mm, "end": v(47.6, 28.79) * mm});
            skArc(sketch, "E179", {"start": v(-53.95, 35.14) * mm, "mid": v(-52.09, 30.65) * mm, "end": v(-47.6, 28.79) * mm});
            skLineSegment(sketch, "E180", {"start": v(-53.95, 54.19) * mm, "end": v(-53.95, 35.14) * mm});
            skArc(sketch, "E181", {"start": v(-47.6, 60.54) * mm, "mid": v(-52.09, 58.68) * mm, "end": v(-53.95, 54.19) * mm});
            skLineSegment(sketch, "E182", {"start": v(47.6, 60.54) * mm, "end": v(-47.6, 60.54) * mm});
            skArc(sketch, "E183", {"start": v(53.95, 54.19) * mm, "mid": v(52.09, 58.68) * mm, "end": v(47.6, 60.54) * mm});
            skLineSegment(sketch, "E184", {"start": v(53.95, 35.14) * mm, "end": v(53.95, 54.19) * mm});
            skArc(sketch, "E185", {"start": v(47.6, 28.79) * mm, "mid": v(52.09, 30.65) * mm, "end": v(53.95, 35.14) * mm});
            skSolve(sketch);
        }
        {
            var Q0;
            Q0=qSketchRegion(id+"F6",true);
            extrude(context, id + "F7", {"entities" : qUnion([Q0]), "depth" : 6.35 * mm});
        }
        {
            var Q0;
            Q0=makeQuery(id+"F7.opExtrude","CAP_FACE",FACE,{"disambiguationData":[OSD([sQuery(id+"F6.wireOp",EDGE,"765eaaff-3c03-4aed-97cd-0da59d786b2a"),sQuery(id+"F6.wireOp",EDGE,"bfbbba31-eefb-4337-b840-f57609f327d5"),sQuery(id+"F6.wireOp",EDGE,"d9fe1464-95a0-43a8-9d73-98f239073346"),sQuery(id+"F6.wireOp",EDGE,"3dbae0e5-671e-48e1-8151-e821474c8e52"),sQuery(id+"F6.wireOp",EDGE,"E106"),sQuery(id+"F6.wireOp",EDGE,"E107"),sQuery(id+"F6.wireOp",EDGE,"E108"),sQuery(id+"F6.wireOp",EDGE,"E109"),sQuery(id+"F6.wireOp",EDGE,"E110"),sQuery(id+"F6.wireOp",EDGE,"E111"),sQuery(id+"F6.wireOp",EDGE,"E112"),sQuery(id+"F6.wireOp",EDGE,"E113"),sQuery(id+"F6.wireOp",EDGE,"E114"),sQuery(id+"F6.wireOp",EDGE,"E115"),sQuery(id+"F6.wireOp",EDGE,"E116"),sQuery(id+"F6.wireOp",EDGE,"E117"),sQuery(id+"F6.wireOp",EDGE,"E118"),sQuery(id+"F6.wireOp",EDGE,"E119"),sQuery(id+"F6.wireOp",EDGE,"E120"),sQuery(id+"F6.wireOp",EDGE,"E121"),sQuery(id+"F6.wireOp",EDGE,"E122"),sQuery(id+"F6.wireOp",EDGE,"E123"),sQuery(id+"F6.wireOp",EDGE,"E124"),sQuery(id+"F6.wireOp",EDGE,"E125"),sQuery(id+"F6.wireOp",EDGE,"E126"),sQuery(id+"F6.wireOp",EDGE,"E127"),sQuery(id+"F6.wireOp",EDGE,"E128"),sQuery(id+"F6.wireOp",EDGE,"E129"),sQuery(id+"F6.wireOp",EDGE,"E130"),sQuery(id+"F6.wireOp",EDGE,"E131"),sQuery(id+"F6.wireOp",EDGE,"E132"),sQuery(id+"F6.wireOp",EDGE,"E133"),sQuery(id+"F6.wireOp",EDGE,"E134"),sQuery(id+"F6.wireOp",EDGE,"E135"),sQuery(id+"F6.wireOp",EDGE,"E136"),sQuery(id+"F6.wireOp",EDGE,"E137"),sQuery(id+"F6.wireOp",EDGE,"E138"),sQuery(id+"F6.wireOp",EDGE,"E139"),sQuery(id+"F6.wireOp",EDGE,"E140"),sQuery(id+"F6.wireOp",EDGE,"E141"),sQuery(id+"F6.wireOp",EDGE,"E142"),sQuery(id+"F6.wireOp",EDGE,"E143"),sQuery(id+"F6.wireOp",EDGE,"E144"),sQuery(id+"F6.wireOp",EDGE,"E145"),sQuery(id+"F6.wireOp",EDGE,"E146"),sQuery(id+"F6.wireOp",EDGE,"E147"),sQuery(id+"F6.wireOp",EDGE,"E148"),sQuery(id+"F6.wireOp",EDGE,"E149"),sQuery(id+"F6.wireOp",EDGE,"E150"),sQuery(id+"F6.wireOp",EDGE,"E151"),sQuery(id+"F6.wireOp",EDGE,"E152"),sQuery(id+"F6.wireOp",EDGE,"E153"),sQuery(id+"F6.wireOp",EDGE,"E154"),sQuery(id+"F6.wireOp",EDGE,"E155"),sQuery(id+"F6.wireOp",EDGE,"E156"),sQuery(id+"F6.wireOp",EDGE,"E157"),sQuery(id+"F6.wireOp",EDGE,"E158"),sQuery(id+"F6.wireOp",EDGE,"E159"),sQuery(id+"F6.wireOp",EDGE,"E160"),sQuery(id+"F6.wireOp",EDGE,"E161"),sQuery(id+"F6.wireOp",EDGE,"E162"),sQuery(id+"F6.wireOp",EDGE,"E163"),sQuery(id+"F6.wireOp",EDGE,"E164"),sQuery(id+"F6.wireOp",EDGE,"E165"),sQuery(id+"F6.wireOp",EDGE,"E166"),sQuery(id+"F6.wireOp",EDGE,"E167"),sQuery(id+"F6.wireOp",EDGE,"E168"),sQuery(id+"F6.wireOp",EDGE,"E169"),sQuery(id+"F6.wireOp",EDGE,"E170"),sQuery(id+"F6.wireOp",EDGE,"E171"),sQuery(id+"F6.wireOp",EDGE,"E172"),sQuery(id+"F6.wireOp",EDGE,"E173"),sQuery(id+"F6.wireOp",EDGE,"E174"),sQuery(id+"F6.wireOp",EDGE,"E175"),sQuery(id+"F6.wireOp",EDGE,"E176"),sQuery(id+"F6.wireOp",EDGE,"E177"),sQuery(id+"F6.wireOp",EDGE,"E178"),sQuery(id+"F6.wireOp",EDGE,"E179"),sQuery(id+"F6.wireOp",EDGE,"E180"),sQuery(id+"F6.wireOp",EDGE,"E181"),sQuery(id+"F6.wireOp",EDGE,"E182"),sQuery(id+"F6.wireOp",EDGE,"E183"),sQuery(id+"F6.wireOp",EDGE,"E184"),sQuery(id+"F6.wireOp",EDGE,"E185"),sQuery(id+"F6.wireOp",EDGE,"f9493e98-5abe-4126-86ac-bdb0b4f7d6da"),sQuery(id+"F6.wireOp",EDGE,"112f2961-29c0-47fd-bd17-f927e6cd5f86"),sQuery(id+"F6.wireOp",EDGE,"d182d45b-51f4-4f19-bbab-538119165d43"),sQuery(id+"F6.wireOp",EDGE,"f2dcc7ce-426b-4624-9908-b4b424994630")])],"isStart":false});
            var sketch = newSketch(context, id + "F8", { "sketchPlane" : qUnion([Q0])});
            skLineSegment(sketch, "E186", {"start": v(225.43, -92.22) * mm, "end": v(47.24, -92.22) * mm, "construction": true});
            skLineSegment(sketch, "E187", {"start": v(47.24, -92.22) * mm, "end": v(11.43, -92.22) * mm, "construction": true});
            skCircle(sketch, "E188", {"center": v(11.43, -92.22) * mm, "radius": 6.35 * mm, "construction": true});
            skLineSegment(sketch, "E189.bottom", {"start": v(-39.37, -76.2) * mm, "end": v(36.83, -76.2) * mm});
            skLineSegment(sketch, "E189.top", {"start": v(-39.37, -101.6) * mm, "end": v(36.83, -101.6) * mm});
            skLineSegment(sketch, "E189.left", {"start": v(-39.37, -76.2) * mm, "end": v(-39.37, -101.6) * mm});
            skLineSegment(sketch, "E189.right", {"start": v(36.83, -76.2) * mm, "end": v(36.83, -101.6) * mm});
            skLineSegment(sketch, "E190", {"start": v(11.43, -92.22) * mm, "end": v(-13.97, -92.22) * mm, "construction": true});
            skCircle(sketch, "E191", {"center": v(-13.97, -92.22) * mm, "radius": 6.35 * mm, "construction": true});
            skSolve(sketch);
        }
        {
            var Q0;
            Q0=qSketchRegion(id+"F8",true);
            extrude(context, id + "F9", {"entities" : qUnion([Q0]), "operationType" : NewBodyOperationType.REMOVE, "oppositeDirection" : true, "depth" : 6.35 * mm});
        }
        {
            var Q0;
            Q0=makeQuery(id+"F7.opExtrude","SWEPT_BODY",BODY,{"disambiguationData":[OSD([sQuery(id+"F6.wireOp",EDGE,"765eaaff-3c03-4aed-97cd-0da59d786b2a"),sQuery(id+"F6.wireOp",EDGE,"bfbbba31-eefb-4337-b840-f57609f327d5"),sQuery(id+"F6.wireOp",EDGE,"d9fe1464-95a0-43a8-9d73-98f239073346"),sQuery(id+"F6.wireOp",EDGE,"3dbae0e5-671e-48e1-8151-e821474c8e52"),sQuery(id+"F6.wireOp",EDGE,"E106"),sQuery(id+"F6.wireOp",EDGE,"E107"),sQuery(id+"F6.wireOp",EDGE,"E108"),sQuery(id+"F6.wireOp",EDGE,"E109"),sQuery(id+"F6.wireOp",EDGE,"E110"),sQuery(id+"F6.wireOp",EDGE,"E111"),sQuery(id+"F6.wireOp",EDGE,"E112"),sQuery(id+"F6.wireOp",EDGE,"E113"),sQuery(id+"F6.wireOp",EDGE,"E114"),sQuery(id+"F6.wireOp",EDGE,"E115"),sQuery(id+"F6.wireOp",EDGE,"E116"),sQuery(id+"F6.wireOp",EDGE,"E117"),sQuery(id+"F6.wireOp",EDGE,"E118"),sQuery(id+"F6.wireOp",EDGE,"E119"),sQuery(id+"F6.wireOp",EDGE,"E120"),sQuery(id+"F6.wireOp",EDGE,"E121"),sQuery(id+"F6.wireOp",EDGE,"E122"),sQuery(id+"F6.wireOp",EDGE,"E123"),sQuery(id+"F6.wireOp",EDGE,"E124"),sQuery(id+"F6.wireOp",EDGE,"E125"),sQuery(id+"F6.wireOp",EDGE,"E126"),sQuery(id+"F6.wireOp",EDGE,"E127"),sQuery(id+"F6.wireOp",EDGE,"E128"),sQuery(id+"F6.wireOp",EDGE,"E129"),sQuery(id+"F6.wireOp",EDGE,"E130"),sQuery(id+"F6.wireOp",EDGE,"E131"),sQuery(id+"F6.wireOp",EDGE,"E132"),sQuery(id+"F6.wireOp",EDGE,"E133"),sQuery(id+"F6.wireOp",EDGE,"E134"),sQuery(id+"F6.wireOp",EDGE,"E135"),sQuery(id+"F6.wireOp",EDGE,"E136"),sQuery(id+"F6.wireOp",EDGE,"E137"),sQuery(id+"F6.wireOp",EDGE,"E138"),sQuery(id+"F6.wireOp",EDGE,"E139"),sQuery(id+"F6.wireOp",EDGE,"E140"),sQuery(id+"F6.wireOp",EDGE,"E141"),sQuery(id+"F6.wireOp",EDGE,"E142"),sQuery(id+"F6.wireOp",EDGE,"E143"),sQuery(id+"F6.wireOp",EDGE,"E144"),sQuery(id+"F6.wireOp",EDGE,"E145"),sQuery(id+"F6.wireOp",EDGE,"E146"),sQuery(id+"F6.wireOp",EDGE,"E147"),sQuery(id+"F6.wireOp",EDGE,"E148"),sQuery(id+"F6.wireOp",EDGE,"E149"),sQuery(id+"F6.wireOp",EDGE,"E150"),sQuery(id+"F6.wireOp",EDGE,"E151"),sQuery(id+"F6.wireOp",EDGE,"E152"),sQuery(id+"F6.wireOp",EDGE,"E153"),sQuery(id+"F6.wireOp",EDGE,"E154"),sQuery(id+"F6.wireOp",EDGE,"E155"),sQuery(id+"F6.wireOp",EDGE,"E156"),sQuery(id+"F6.wireOp",EDGE,"E157"),sQuery(id+"F6.wireOp",EDGE,"E158"),sQuery(id+"F6.wireOp",EDGE,"E159"),sQuery(id+"F6.wireOp",EDGE,"E160"),sQuery(id+"F6.wireOp",EDGE,"E161"),sQuery(id+"F6.wireOp",EDGE,"E162"),sQuery(id+"F6.wireOp",EDGE,"E163"),sQuery(id+"F6.wireOp",EDGE,"E164"),sQuery(id+"F6.wireOp",EDGE,"E165"),sQuery(id+"F6.wireOp",EDGE,"E166"),sQuery(id+"F6.wireOp",EDGE,"E167"),sQuery(id+"F6.wireOp",EDGE,"E168"),sQuery(id+"F6.wireOp",EDGE,"E169"),sQuery(id+"F6.wireOp",EDGE,"E170"),sQuery(id+"F6.wireOp",EDGE,"E171"),sQuery(id+"F6.wireOp",EDGE,"E172"),sQuery(id+"F6.wireOp",EDGE,"E173"),sQuery(id+"F6.wireOp",EDGE,"E174"),sQuery(id+"F6.wireOp",EDGE,"E175"),sQuery(id+"F6.wireOp",EDGE,"E176"),sQuery(id+"F6.wireOp",EDGE,"E177"),sQuery(id+"F6.wireOp",EDGE,"E178"),sQuery(id+"F6.wireOp",EDGE,"E179"),sQuery(id+"F6.wireOp",EDGE,"E180"),sQuery(id+"F6.wireOp",EDGE,"E181"),sQuery(id+"F6.wireOp",EDGE,"E182"),sQuery(id+"F6.wireOp",EDGE,"E183"),sQuery(id+"F6.wireOp",EDGE,"E184"),sQuery(id+"F6.wireOp",EDGE,"E185"),sQuery(id+"F6.wireOp",EDGE,"f9493e98-5abe-4126-86ac-bdb0b4f7d6da"),sQuery(id+"F6.wireOp",EDGE,"112f2961-29c0-47fd-bd17-f927e6cd5f86"),sQuery(id+"F6.wireOp",EDGE,"d182d45b-51f4-4f19-bbab-538119165d43"),sQuery(id+"F6.wireOp",EDGE,"f2dcc7ce-426b-4624-9908-b4b424994630")])]});
            var Q1;
            Q1=qCreatedBy(id+"F5.planeOp",FACE);
            mirror(context, id + "F10", {"entities" : qUnion([Q0]), "mirrorPlane" : qUnion([Q1])});
        }
        {
            var Q0;
            Q0=makeQuery(id+"F10.opPattern","COPY",FACE,{"derivedFrom":makeQuery(id+"F7.opExtrude","CAP_FACE",FACE,{"disambiguationData":[OSD([sQuery(id+"F6.wireOp",EDGE,"765eaaff-3c03-4aed-97cd-0da59d786b2a"),sQuery(id+"F6.wireOp",EDGE,"bfbbba31-eefb-4337-b840-f57609f327d5"),sQuery(id+"F6.wireOp",EDGE,"d9fe1464-95a0-43a8-9d73-98f239073346"),sQuery(id+"F6.wireOp",EDGE,"3dbae0e5-671e-48e1-8151-e821474c8e52"),sQuery(id+"F6.wireOp",EDGE,"E106"),sQuery(id+"F6.wireOp",EDGE,"E107"),sQuery(id+"F6.wireOp",EDGE,"E108"),sQuery(id+"F6.wireOp",EDGE,"E109"),sQuery(id+"F6.wireOp",EDGE,"E110"),sQuery(id+"F6.wireOp",EDGE,"E111"),sQuery(id+"F6.wireOp",EDGE,"E112"),sQuery(id+"F6.wireOp",EDGE,"E113"),sQuery(id+"F6.wireOp",EDGE,"E114"),sQuery(id+"F6.wireOp",EDGE,"E115"),sQuery(id+"F6.wireOp",EDGE,"E116"),sQuery(id+"F6.wireOp",EDGE,"E117"),sQuery(id+"F6.wireOp",EDGE,"E118"),sQuery(id+"F6.wireOp",EDGE,"E119"),sQuery(id+"F6.wireOp",EDGE,"E120"),sQuery(id+"F6.wireOp",EDGE,"E121"),sQuery(id+"F6.wireOp",EDGE,"E122"),sQuery(id+"F6.wireOp",EDGE,"E123"),sQuery(id+"F6.wireOp",EDGE,"E124"),sQuery(id+"F6.wireOp",EDGE,"E125"),sQuery(id+"F6.wireOp",EDGE,"E126"),sQuery(id+"F6.wireOp",EDGE,"E127"),sQuery(id+"F6.wireOp",EDGE,"E128"),sQuery(id+"F6.wireOp",EDGE,"E129"),sQuery(id+"F6.wireOp",EDGE,"E130"),sQuery(id+"F6.wireOp",EDGE,"E131"),sQuery(id+"F6.wireOp",EDGE,"E132"),sQuery(id+"F6.wireOp",EDGE,"E133"),sQuery(id+"F6.wireOp",EDGE,"E134"),sQuery(id+"F6.wireOp",EDGE,"E135"),sQuery(id+"F6.wireOp",EDGE,"E136"),sQuery(id+"F6.wireOp",EDGE,"E137"),sQuery(id+"F6.wireOp",EDGE,"E138"),sQuery(id+"F6.wireOp",EDGE,"E139"),sQuery(id+"F6.wireOp",EDGE,"E140"),sQuery(id+"F6.wireOp",EDGE,"E141"),sQuery(id+"F6.wireOp",EDGE,"E142"),sQuery(id+"F6.wireOp",EDGE,"E143"),sQuery(id+"F6.wireOp",EDGE,"E144"),sQuery(id+"F6.wireOp",EDGE,"E145"),sQuery(id+"F6.wireOp",EDGE,"E146"),sQuery(id+"F6.wireOp",EDGE,"E147"),sQuery(id+"F6.wireOp",EDGE,"E148"),sQuery(id+"F6.wireOp",EDGE,"E149"),sQuery(id+"F6.wireOp",EDGE,"E150"),sQuery(id+"F6.wireOp",EDGE,"E151"),sQuery(id+"F6.wireOp",EDGE,"E152"),sQuery(id+"F6.wireOp",EDGE,"E153"),sQuery(id+"F6.wireOp",EDGE,"E154"),sQuery(id+"F6.wireOp",EDGE,"E155"),sQuery(id+"F6.wireOp",EDGE,"E156"),sQuery(id+"F6.wireOp",EDGE,"E157"),sQuery(id+"F6.wireOp",EDGE,"E158"),sQuery(id+"F6.wireOp",EDGE,"E159"),sQuery(id+"F6.wireOp",EDGE,"E160"),sQuery(id+"F6.wireOp",EDGE,"E161"),sQuery(id+"F6.wireOp",EDGE,"E162"),sQuery(id+"F6.wireOp",EDGE,"E163"),sQuery(id+"F6.wireOp",EDGE,"E164"),sQuery(id+"F6.wireOp",EDGE,"E165"),sQuery(id+"F6.wireOp",EDGE,"E166"),sQuery(id+"F6.wireOp",EDGE,"E167"),sQuery(id+"F6.wireOp",EDGE,"E168"),sQuery(id+"F6.wireOp",EDGE,"E169"),sQuery(id+"F6.wireOp",EDGE,"E170"),sQuery(id+"F6.wireOp",EDGE,"E171"),sQuery(id+"F6.wireOp",EDGE,"E172"),sQuery(id+"F6.wireOp",EDGE,"E173"),sQuery(id+"F6.wireOp",EDGE,"E174"),sQuery(id+"F6.wireOp",EDGE,"E175"),sQuery(id+"F6.wireOp",EDGE,"E176"),sQuery(id+"F6.wireOp",EDGE,"E177"),sQuery(id+"F6.wireOp",EDGE,"E178"),sQuery(id+"F6.wireOp",EDGE,"E179"),sQuery(id+"F6.wireOp",EDGE,"E180"),sQuery(id+"F6.wireOp",EDGE,"E181"),sQuery(id+"F6.wireOp",EDGE,"E182"),sQuery(id+"F6.wireOp",EDGE,"E183"),sQuery(id+"F6.wireOp",EDGE,"E184"),sQuery(id+"F6.wireOp",EDGE,"E185"),sQuery(id+"F6.wireOp",EDGE,"f9493e98-5abe-4126-86ac-bdb0b4f7d6da"),sQuery(id+"F6.wireOp",EDGE,"112f2961-29c0-47fd-bd17-f927e6cd5f86"),sQuery(id+"F6.wireOp",EDGE,"d182d45b-51f4-4f19-bbab-538119165d43"),sQuery(id+"F6.wireOp",EDGE,"f2dcc7ce-426b-4624-9908-b4b424994630")])],"isStart":false}),"instanceName":"1"});
            cPlane(context, id + "F11", {"entities" : qUnion([Q0]), "cplaneType" : CPlaneType.OFFSET, "offset" : 0 * mm, "width" : 152.4 * mm, "height" : 152.4 * mm});
        }
        {
            var Q0;
            Q0=qCreatedBy(id+"F11.planeOp",FACE);
            var sketch = newSketch(context, id + "F12", { "sketchPlane" : qUnion([Q0])});
            skLineSegment(sketch, "E192", {"start": v(122.27, 73.06) * mm, "end": v(89.92, 75.84) * mm});
            skPoint(sketch, "E192.endSnap0", {"position": v(89.92, 75.87) * mm});
            skLineSegment(sketch, "E193", {"start": v(89.92, 75.84) * mm, "end": v(99.44, 97.3) * mm});
            skLineSegment(sketch, "E194", {"start": v(99.44, 97.3) * mm, "end": v(119.46, 93.1) * mm});
            skLineSegment(sketch, "E195", {"start": v(119.46, 93.1) * mm, "end": v(122.27, 73.06) * mm});
            skSolve(sketch);
        }
        {
            var Q0;
            Q0=qSketchRegion(id+"F12",true);
            extrude(context, id + "F13", {"entities" : qUnion([Q0]), "operationType" : NewBodyOperationType.REMOVE, "endBound" : BoundingType.THROUGH_ALL, "oppositeDirection" : true, "depth" : 70.87 * mm});
        }
        {
            var Q0;
            Q0=makeQuery(id+"F4.opExtrude","CAP_FACE",FACE,{"disambiguationData":[OSD([sQuery(id+"F3.wireOp",EDGE,"E98"),sQuery(id+"F3.wireOp",EDGE,"E99"),sQuery(id+"F3.wireOp",EDGE,"E100"),sQuery(id+"F3.wireOp",EDGE,"E101"),sQuery(id+"F3.wireOp",EDGE,"E102"),sQuery(id+"F3.wireOp",EDGE,"E103"),sQuery(id+"F3.wireOp",EDGE,"E104"),sQuery(id+"F3.wireOp",EDGE,"E105")])],"isStart":false});
            var sketch = newSketch(context, id + "F14", { "sketchPlane" : qUnion([Q0])});
            skLineSegment(sketch, "E196.bottom", {"start": v(-225.43, -101.6) * mm, "end": v(-36.83, -101.6) * mm});
            skLineSegment(sketch, "E196.top", {"start": v(-225.43, -127) * mm, "end": v(225.43, -127) * mm});
            skLineSegment(sketch, "E196.left", {"start": v(-225.43, -101.6) * mm, "end": v(-225.43, -127) * mm});
            skLineSegment(sketch, "E196.right", {"start": v(225.43, -101.6) * mm, "end": v(225.43, -127) * mm});
            skLineSegment(sketch, "E197.bottom", {"start": v(-36.83, -76.2) * mm, "end": v(39.37, -76.2) * mm});
            skLineSegment(sketch, "E197.left", {"start": v(-36.83, -76.2) * mm, "end": v(-36.83, -101.6) * mm});
            skLineSegment(sketch, "E197.right", {"start": v(39.37, -76.2) * mm, "end": v(39.37, -101.6) * mm});
            skLineSegment(sketch, "E198.trimOffspring", {"start": v(39.37, -101.6) * mm, "end": v(225.43, -101.6) * mm});
            skSolve(sketch);
        }
        {
            var Q0;
            Q0=qSketchRegion(id+"F14",true);
            extrude(context, id + "F15", {"entities" : qUnion([Q0]), "depth" : 6.35 * mm});
        }
        {
            var Q0;
            Q0=makeQuery(id+"F15.opExtrude","CAP_FACE",FACE,{"disambiguationData":[OSD([sQuery(id+"F14.wireOp",EDGE,"E196.bottom"),sQuery(id+"F14.wireOp",EDGE,"E196.top"),sQuery(id+"F14.wireOp",EDGE,"E196.left"),sQuery(id+"F14.wireOp",EDGE,"E196.right"),sQuery(id+"F14.wireOp",EDGE,"E197.bottom"),sQuery(id+"F14.wireOp",EDGE,"E197.left"),sQuery(id+"F14.wireOp",EDGE,"E197.right"),sQuery(id+"F14.wireOp",EDGE,"E198.trimOffspring")])],"isStart":false});
            var sketch = newSketch(context, id + "F16", { "sketchPlane" : qUnion([Q0])});
            skLineSegment(sketch, "E199.bottom", {"start": v(-225.43, -101.6) * mm, "end": v(-196.22, -101.6) * mm});
            skLineSegment(sketch, "E199.top", {"start": v(-225.43, -127) * mm, "end": v(225.43, -127) * mm});
            skLineSegment(sketch, "E199.left", {"start": v(-225.43, -101.6) * mm, "end": v(-225.43, -127) * mm});
            skLineSegment(sketch, "E199.right", {"start": v(225.43, -101.6) * mm, "end": v(225.43, -127) * mm});
            skLineSegment(sketch, "E200.left", {"start": v(-196.22, -101.6) * mm, "end": v(-196.22, -91.44) * mm});
            skLineSegment(sketch, "E200.right", {"start": v(196.22, -101.6) * mm, "end": v(196.22, -91.44) * mm});
            skLineSegment(sketch, "E201.top", {"start": v(-208.92, -91.44) * mm, "end": v(-196.22, -91.44) * mm});
            skLineSegment(sketch, "E201.left", {"start": v(-208.92, -54.61) * mm, "end": v(-208.92, -91.44) * mm});
            skLineSegment(sketch, "E202.top", {"start": v(196.22, -91.44) * mm, "end": v(208.92, -91.44) * mm});
            skLineSegment(sketch, "E202.right", {"start": v(208.92, -54.61) * mm, "end": v(208.92, -91.44) * mm});
            skLineSegment(sketch, "E203.bottom", {"start": v(149.86, -11.94) * mm, "end": v(167.64, -11.94) * mm});
            skLineSegment(sketch, "E203.left", {"start": v(149.86, -11.94) * mm, "end": v(149.86, -54.6) * mm});
            skLineSegment(sketch, "E203.right", {"start": v(167.64, -11.94) * mm, "end": v(167.64, -54.61) * mm});
            skLineSegment(sketch, "E204.bottom", {"start": v(-167.9, -11.94) * mm, "end": v(-150.11, -11.94) * mm});
            skLineSegment(sketch, "E204.left", {"start": v(-167.9, -11.94) * mm, "end": v(-167.9, -54.61) * mm});
            skLineSegment(sketch, "E204.right", {"start": v(-150.11, -11.94) * mm, "end": v(-150.11, -54.61) * mm});
            skLineSegment(sketch, "E205.trimOffspring", {"start": v(-150.11, -54.61) * mm, "end": v(149.86, -54.6) * mm});
            skLineSegment(sketch, "E206.trimOffspring", {"start": v(196.22, -101.6) * mm, "end": v(225.43, -101.6) * mm});
            skLineSegment(sketch, "E207", {"start": v(-208.92, -54.61) * mm, "end": v(-167.9, -54.61) * mm});
            skLineSegment(sketch, "E208", {"start": v(208.92, -54.61) * mm, "end": v(167.64, -54.61) * mm});
            skSolve(sketch);
        }
        {
            var Q0;
            Q0=qSketchRegion(id+"F16",true);
            extrude(context, id + "F17", {"entities" : qUnion([Q0]), "depth" : 6.35 * mm});
        }
    });
